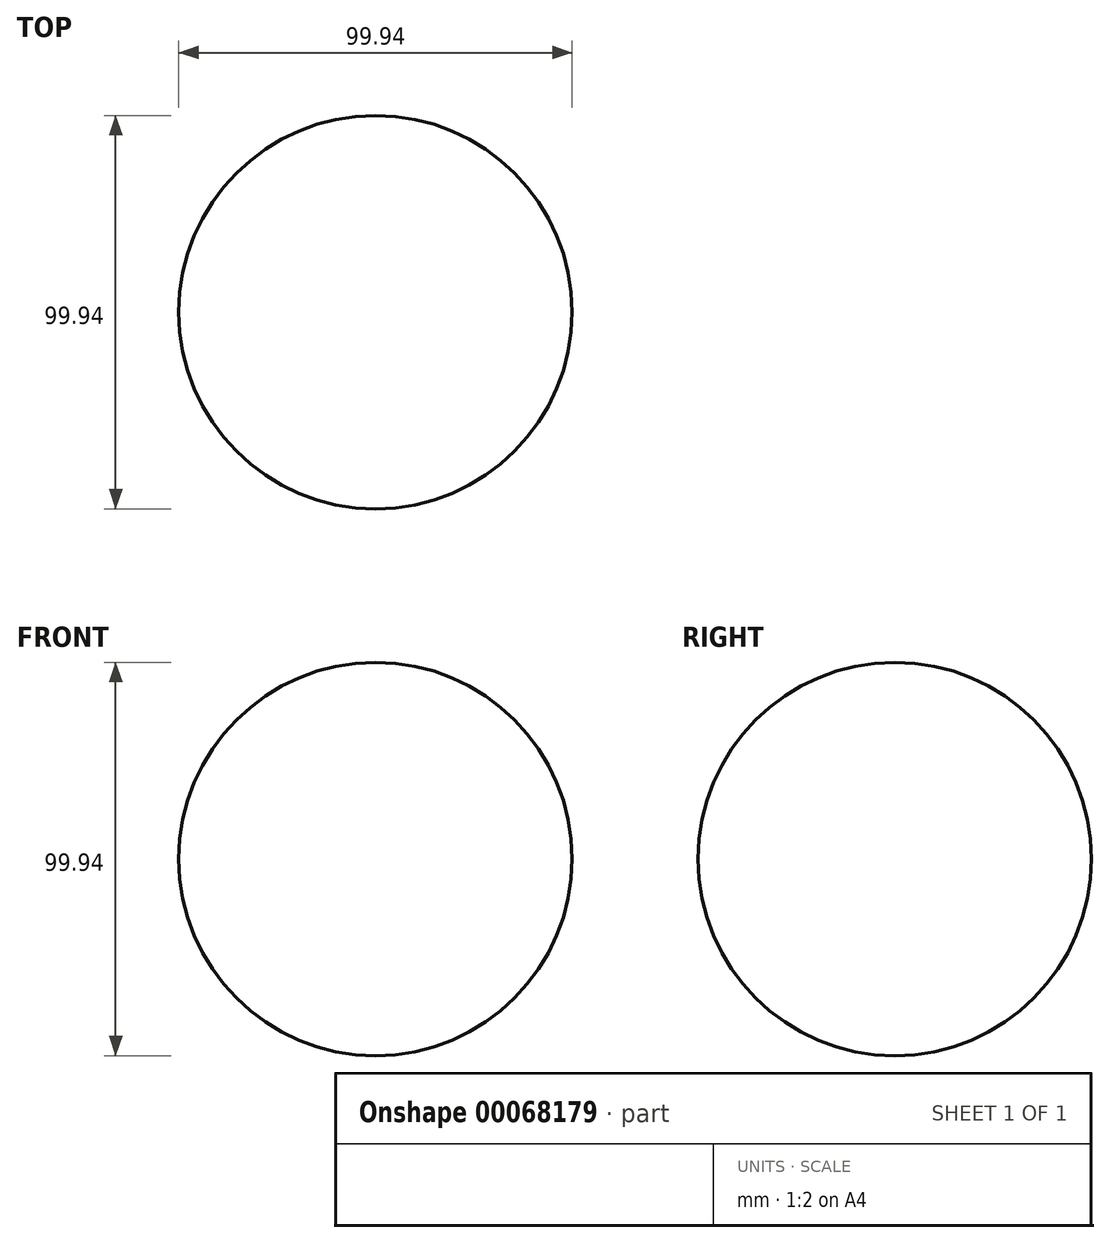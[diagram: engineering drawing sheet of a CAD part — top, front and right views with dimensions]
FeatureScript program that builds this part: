
annotation { "Feature Type Name" : "Feature", "Feature Type Description" : "" }
export const myFeature = defineFeature(function(context is Context, id is Id, definition is map)
    precondition{}
    {
        {
            var Q0;
            Q0=qCreatedBy(makeId("Front.planeOp"),FACE);
            var sketch = newSketch(context, id + "F0", { "sketchPlane" : qUnion([Q0])});
            skArc(sketch, "E0", {"start": v(0, -49.97) * mm, "mid": v(49.97, 0) * mm, "end": v(0, 49.97) * mm});
            skLineSegment(sketch, "E1", {"start": v(0, 49.97) * mm, "end": v(0, -49.97) * mm});
            skSolve(sketch);
        }
        {
            var Q0;
            Q0=makeQuery(id+"F0.imprint","IMPRINT",FACE,{"disambiguationData":[TD([[makeQuery(id+"F0.imprint","IMPRINT",EDGE,{"derivedFrom":sQuery(id+"F0.wireOp",EDGE,"E0")}),1.0]])]});
            var Q1;
            Q1=sQuery(id+"F0.wireOp",EDGE,"E1");
            revolve(context, id + "F1", {"entities" : qUnion([Q0]), "axis" : qUnion([Q1]), "revolveType" : RevolveType.FULL});
        }
    });
